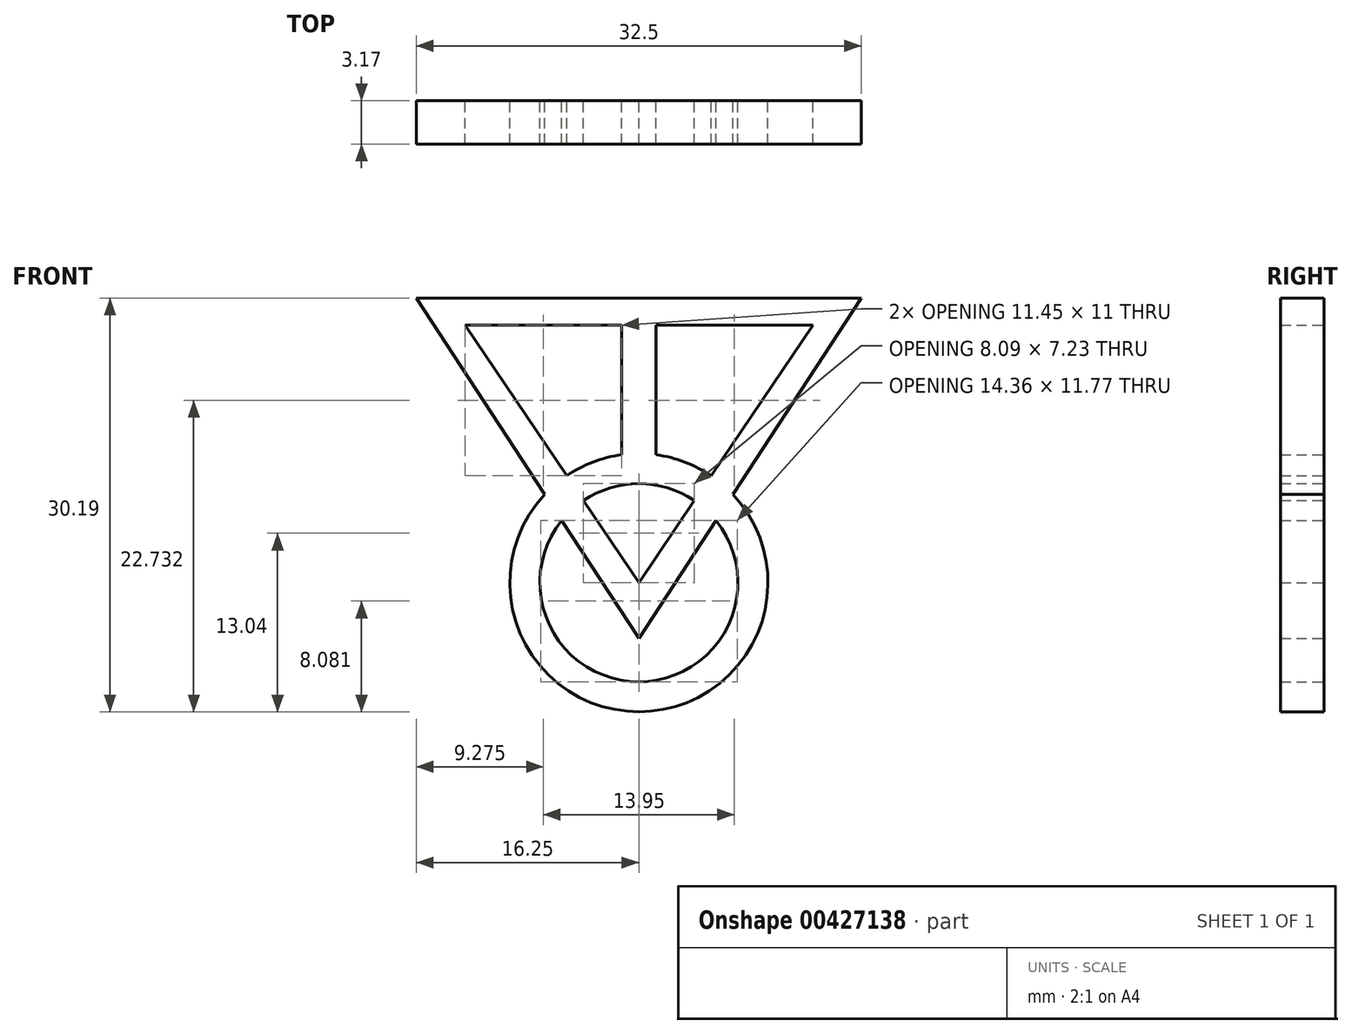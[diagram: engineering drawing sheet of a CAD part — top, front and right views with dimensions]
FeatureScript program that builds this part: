
annotation { "Feature Type Name" : "Feature", "Feature Type Description" : "" }
export const myFeature = defineFeature(function(context is Context, id is Id, definition is map)
    precondition{}
    {
        {
            var Q0;
            Q0=qCreatedBy(makeId("Front.planeOp"),FACE);
            var sketch = newSketch(context, id + "F0", { "sketchPlane" : qUnion([Q0])});
            skLineSegment(sketch, "E0", {"start": v(0, 0) * mm, "end": v(12.7, 0) * mm});
            skLineSegment(sketch, "E1", {"start": v(0, 0) * mm, "end": v(-12.7, 0) * mm});
            skLineSegment(sketch, "E2", {"start": v(0, 0) * mm, "end": v(0, 1.96) * mm});
            skLineSegment(sketch, "E3", {"start": v(0, 1.96) * mm, "end": v(-16.25, 1.96) * mm});
            skLineSegment(sketch, "E4", {"start": v(0, 1.96) * mm, "end": v(16.25, 1.96) * mm});
            skLineSegment(sketch, "E5", {"start": v(-12.7, 0) * mm, "end": v(0, -18.8) * mm});
            skLineSegment(sketch, "E6", {"start": v(0, -18.8) * mm, "end": v(12.7, 0) * mm});
            skLineSegment(sketch, "E7", {"start": v(0, -18.8) * mm, "end": v(0, -22.86) * mm});
            skLineSegment(sketch, "E8", {"start": v(0, -22.86) * mm, "end": v(-16.25, 1.96) * mm});
            skLineSegment(sketch, "E9", {"start": v(0, -22.86) * mm, "end": v(16.25, 1.96) * mm});
            skLineSegment(sketch, "E10", {"start": v(-16.25, 1.96) * mm, "end": v(-12.7, 0) * mm});
            skLineSegment(sketch, "E11", {"start": v(12.7, 0) * mm, "end": v(16.25, 1.96) * mm});
            skLineSegment(sketch, "E12", {"start": v(-1.25, -16.95) * mm, "end": v(-1.25, 0) * mm});
            skLineSegment(sketch, "E13", {"start": v(1.25, -16.95) * mm, "end": v(1.25, 0) * mm});
            skCircle(sketch, "E14", {"center": v(0, -18.8) * mm, "radius": 7.23 * mm});
            skCircle(sketch, "E15", {"center": v(0, -18.8) * mm, "radius": 9.42 * mm});
            skSolve(sketch);
        }
        {
            var Q0;
            {var subQ0=sQuery(id+"F0.wireOp",EDGE,"E2");Q0=makeQuery(id+"F0.imprint","IMPRINT",FACE,{"disambiguationData":[TD([[makeQuery(id+"F0.imprint","IMPRINT",EDGE,{"derivedFrom":subQ0}),1.0]])]});}
            var Q1;
            {var subQ0=sQuery(id+"F0.wireOp",EDGE,"E2");Q1=makeQuery(id+"F0.imprint","IMPRINT",FACE,{"disambiguationData":[TD([[makeQuery(id+"F0.imprint","IMPRINT",EDGE,{"derivedFrom":subQ0}),-1.0]])]});}
            var Q2;
            {var subQ0=sQuery(id+"F0.wireOp",EDGE,"E11");Q2=makeQuery(id+"F0.imprint","IMPRINT",FACE,{"disambiguationData":[TD([[makeQuery(id+"F0.imprint","IMPRINT",EDGE,{"derivedFrom":subQ0}),-1.0]])]});}
            var Q3;
            {var subQ0=sQuery(id+"F0.wireOp",EDGE,"E10");Q3=makeQuery(id+"F0.imprint","IMPRINT",FACE,{"disambiguationData":[TD([[makeQuery(id+"F0.imprint","IMPRINT",EDGE,{"derivedFrom":subQ0}),-1.0]])]});}
            var Q4;
            {var subQ5=sQuery(id+"F0.wireOp",EDGE,"E12");var subQ6=sQuery(id+"F0.wireOp",EDGE,"E1");var subQ7=makeQuery(id+"F0.imprint","INTERSECT",VERTEX,{"derivedFrom":[subQ6,subQ5]});Q4=makeQuery(id+"F0.imprint","IMPRINT",FACE,{"disambiguationData":[TD([[makeQuery(id+"F0.imprint","IMPRINT",EDGE,{"disambiguationData":[TD([[subQ7,1.0]])],"derivedFrom":subQ5}),-1.0]])]});}
            var Q5;
            {var subQ0=sQuery(id+"F0.wireOp",EDGE,"E14");var subQ1=sQuery(id+"F0.wireOp",EDGE,"E12");var subQ2=makeQuery(id+"F0.imprint","INTERSECT",VERTEX,{"derivedFrom":[subQ1,subQ0]});Q5=makeQuery(id+"F0.imprint","IMPRINT",FACE,{"disambiguationData":[TD([[makeQuery(id+"F0.imprint","IMPRINT",EDGE,{"disambiguationData":[TD([[subQ2,-1.0]])],"derivedFrom":subQ1}),-1.0]])]});}
            var Q6;
            {var subQ0=sQuery(id+"F0.wireOp",EDGE,"E15");var subQ1=sQuery(id+"F0.wireOp",EDGE,"E5");var subQ2=makeQuery(id+"F0.imprint","INTERSECT",VERTEX,{"derivedFrom":[subQ1,subQ0]});Q6=makeQuery(id+"F0.imprint","IMPRINT",FACE,{"disambiguationData":[TD([[makeQuery(id+"F0.imprint","IMPRINT",EDGE,{"disambiguationData":[TD([[subQ2,-1.0]])],"derivedFrom":subQ1}),1.0]])]});}
            var Q7;
            {var subQ0=sQuery(id+"F0.wireOp",EDGE,"E15");var subQ1=sQuery(id+"F0.wireOp",EDGE,"E5");var subQ2=makeQuery(id+"F0.imprint","INTERSECT",VERTEX,{"derivedFrom":[subQ1,subQ0]});Q7=makeQuery(id+"F0.imprint","IMPRINT",FACE,{"disambiguationData":[TD([[makeQuery(id+"F0.imprint","IMPRINT",EDGE,{"disambiguationData":[TD([[subQ2,-1.0]])],"derivedFrom":subQ1}),-1.0]])]});}
            var Q8;
            {var subQ0=sQuery(id+"F0.wireOp",EDGE,"E15");var subQ1=sQuery(id+"F0.wireOp",EDGE,"E8");var subQ2=makeQuery(id+"F0.imprint","INTERSECT",VERTEX,{"derivedFrom":[subQ1,subQ0]});Q8=makeQuery(id+"F0.imprint","IMPRINT",FACE,{"disambiguationData":[TD([[makeQuery(id+"F0.imprint","IMPRINT",EDGE,{"disambiguationData":[TD([[subQ2,1.0]])],"derivedFrom":subQ1}),1.0]])]});}
            var Q9;
            {var subQ1=sQuery(id+"F0.wireOp",EDGE,"E7");Q9=makeQuery(id+"F0.imprint","IMPRINT",FACE,{"disambiguationData":[TD([[makeQuery(id+"F0.imprint","IMPRINT",EDGE,{"derivedFrom":subQ1}),-1.0]])]});}
            var Q10;
            {var subQ1=sQuery(id+"F0.wireOp",EDGE,"E7");Q10=makeQuery(id+"F0.imprint","IMPRINT",FACE,{"disambiguationData":[TD([[makeQuery(id+"F0.imprint","IMPRINT",EDGE,{"derivedFrom":subQ1}),1.0]])]});}
            var Q11;
            {var subQ0=sQuery(id+"F0.wireOp",EDGE,"E14");var subQ1=sQuery(id+"F0.wireOp",EDGE,"E6");var subQ2=makeQuery(id+"F0.imprint","INTERSECT",VERTEX,{"derivedFrom":[subQ1,subQ0]});Q11=makeQuery(id+"F0.imprint","IMPRINT",FACE,{"disambiguationData":[TD([[makeQuery(id+"F0.imprint","IMPRINT",EDGE,{"disambiguationData":[TD([[subQ2,-1.0]])],"derivedFrom":subQ1}),1.0]])]});}
            var Q12;
            {var subQ0=sQuery(id+"F0.wireOp",EDGE,"E14");var subQ1=sQuery(id+"F0.wireOp",EDGE,"E6");var subQ2=makeQuery(id+"F0.imprint","INTERSECT",VERTEX,{"derivedFrom":[subQ1,subQ0]});Q12=makeQuery(id+"F0.imprint","IMPRINT",FACE,{"disambiguationData":[TD([[makeQuery(id+"F0.imprint","IMPRINT",EDGE,{"disambiguationData":[TD([[subQ2,-1.0]])],"derivedFrom":subQ1}),-1.0]])]});}
            extrude(context, id + "F1", {"entities" : qUnion([Q0, Q1, Q2, Q3, Q4, Q5, Q6, Q7, Q8, Q9, Q10, Q11, Q12]), "depth" : 3.17 * mm});
        }
    });
